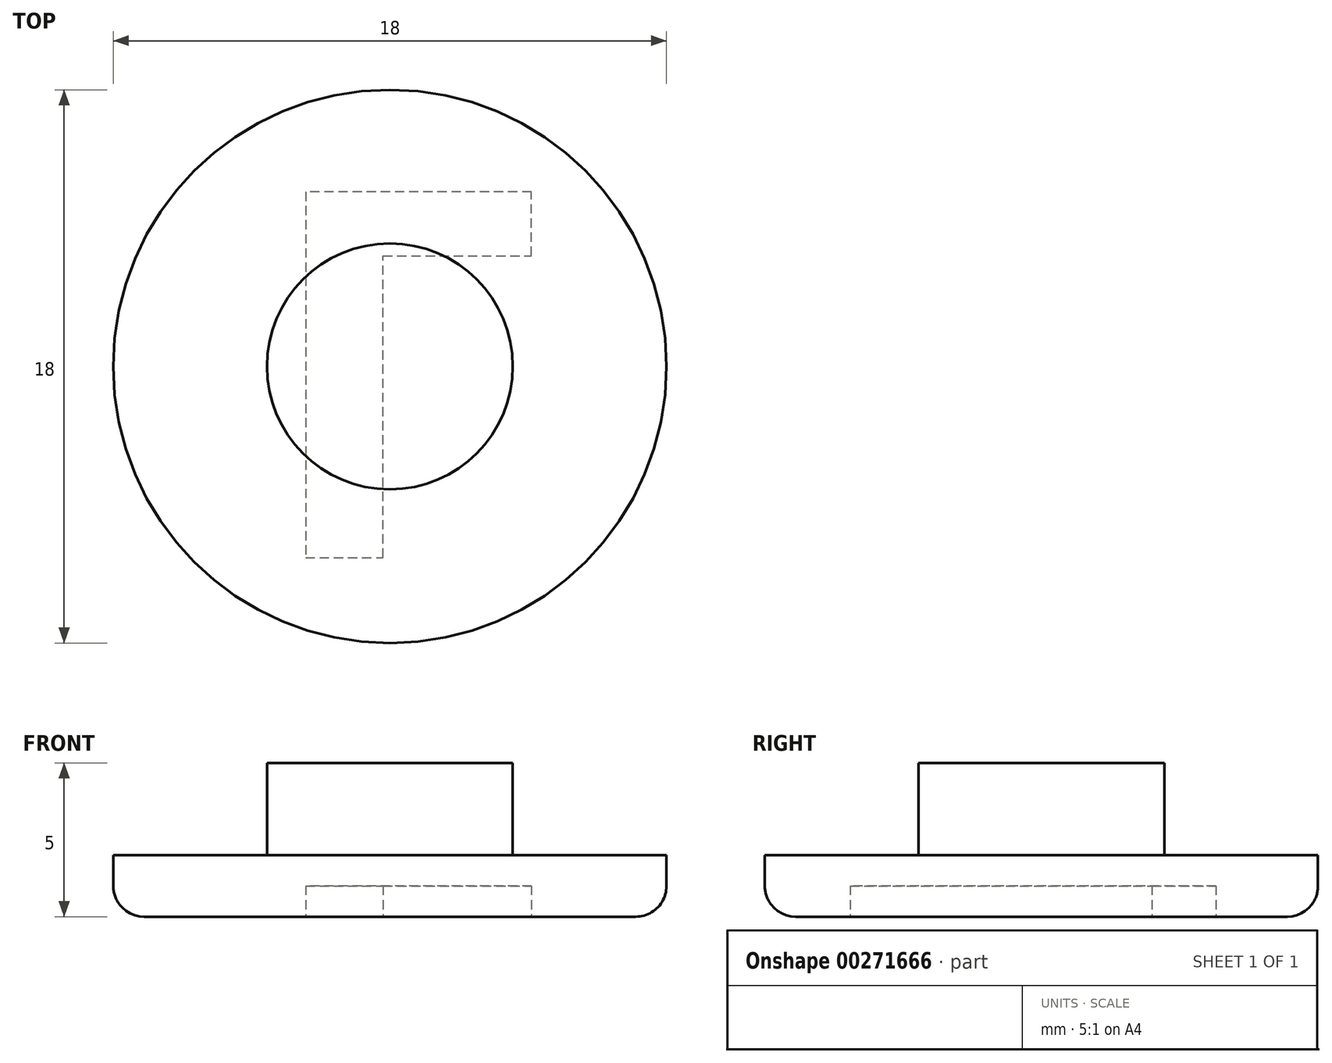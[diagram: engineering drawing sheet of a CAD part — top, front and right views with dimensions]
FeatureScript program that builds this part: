
annotation { "Feature Type Name" : "Feature", "Feature Type Description" : "" }
export const myFeature = defineFeature(function(context is Context, id is Id, definition is map)
    precondition{}
    {
        {
            var Q0;
            Q0=qCreatedBy(makeId("Top.planeOp"),FACE);
            var sketch = newSketch(context, id + "F0", { "sketchPlane" : qUnion([Q0])});
            skCircle(sketch, "E0", {"center": v(0, 0) * mm, "radius": 9 * mm});
            skSolve(sketch);
        }
        {
            var Q0;
            Q0=makeQuery(id+"F0.imprint","IMPRINT",FACE,{"disambiguationData":[TD([[makeQuery(id+"F0.imprint","IMPRINT",EDGE,{"derivedFrom":sQuery(id+"F0.wireOp",EDGE,"E0")}),1.0]])]});
            extrude(context, id + "F1", {"entities" : qUnion([Q0]), "depth" : 2 * mm});
        }
        {
            var Q0;
            Q0=makeQuery(id+"F1.opExtrude","CAP_FACE",FACE,{"disambiguationData":[OSD([sQuery(id+"F0.wireOp",EDGE,"E0")])],"isStart":false});
            var sketch = newSketch(context, id + "F2", { "sketchPlane" : qUnion([Q0])});
            skCircle(sketch, "E1", {"center": v(0, 0) * mm, "radius": 4 * mm});
            skSolve(sketch);
        }
        {
            var Q0;
            Q0=makeQuery(id+"F2.imprint","IMPRINT",FACE,{"disambiguationData":[TD([[makeQuery(id+"F2.imprint","IMPRINT",EDGE,{"derivedFrom":sQuery(id+"F2.wireOp",EDGE,"E1")}),1.0]])]});
            extrude(context, id + "F3", {"entities" : qUnion([Q0]), "operationType" : NewBodyOperationType.ADD, "depth" : 3 * mm});
        }
        {
            var Q0;
            Q0=makeQuery(id+"F1.opExtrude","CAP_EDGE",EDGE,{"disambiguationData":[OSD([sQuery(id+"F0.wireOp",EDGE,"E0")])],"isStart":true});
            fillet(context, id + "F4", {"entities" : qUnion([Q0]), "radius" : 1 * mm, "tangentPropagation" : true, "allowEdgeOverflow" : false});
        }
        {
            var Q0;
            Q0=makeQuery(id+"F1.opExtrude","CAP_FACE",FACE,{"disambiguationData":[OSD([sQuery(id+"F0.wireOp",EDGE,"E0")])],"isStart":true});
            var sketch = newSketch(context, id + "F5", { "sketchPlane" : qUnion([Q0])});
            skText(sketch, "E2", { "text": "L", "fontName": "OpenSans-Bold.ttf"});
            const initialGuessF5  = {"E2": [-0.00424, -0.00568, 1, 0, 0.012]};
            skSetInitialGuess(sketch, initialGuessF5);
            skSolve(sketch);
        }
        {
            var Q0;
            Q0=makeQuery(id+"F5.imprint","IMPRINT",FACE,{"disambiguationData":[TD([[makeQuery(id+"F5.imprint","IMPRINT",EDGE,{"derivedFrom":sQuery(id+"F5.wireOp",EDGE,"E2.sketch_text.stroke-0")}),-1.0]])]});
            extrude(context, id + "F6", {"entities" : qUnion([Q0]), "operationType" : NewBodyOperationType.REMOVE, "oppositeDirection" : true, "depth" : 1 * mm});
        }
    });
